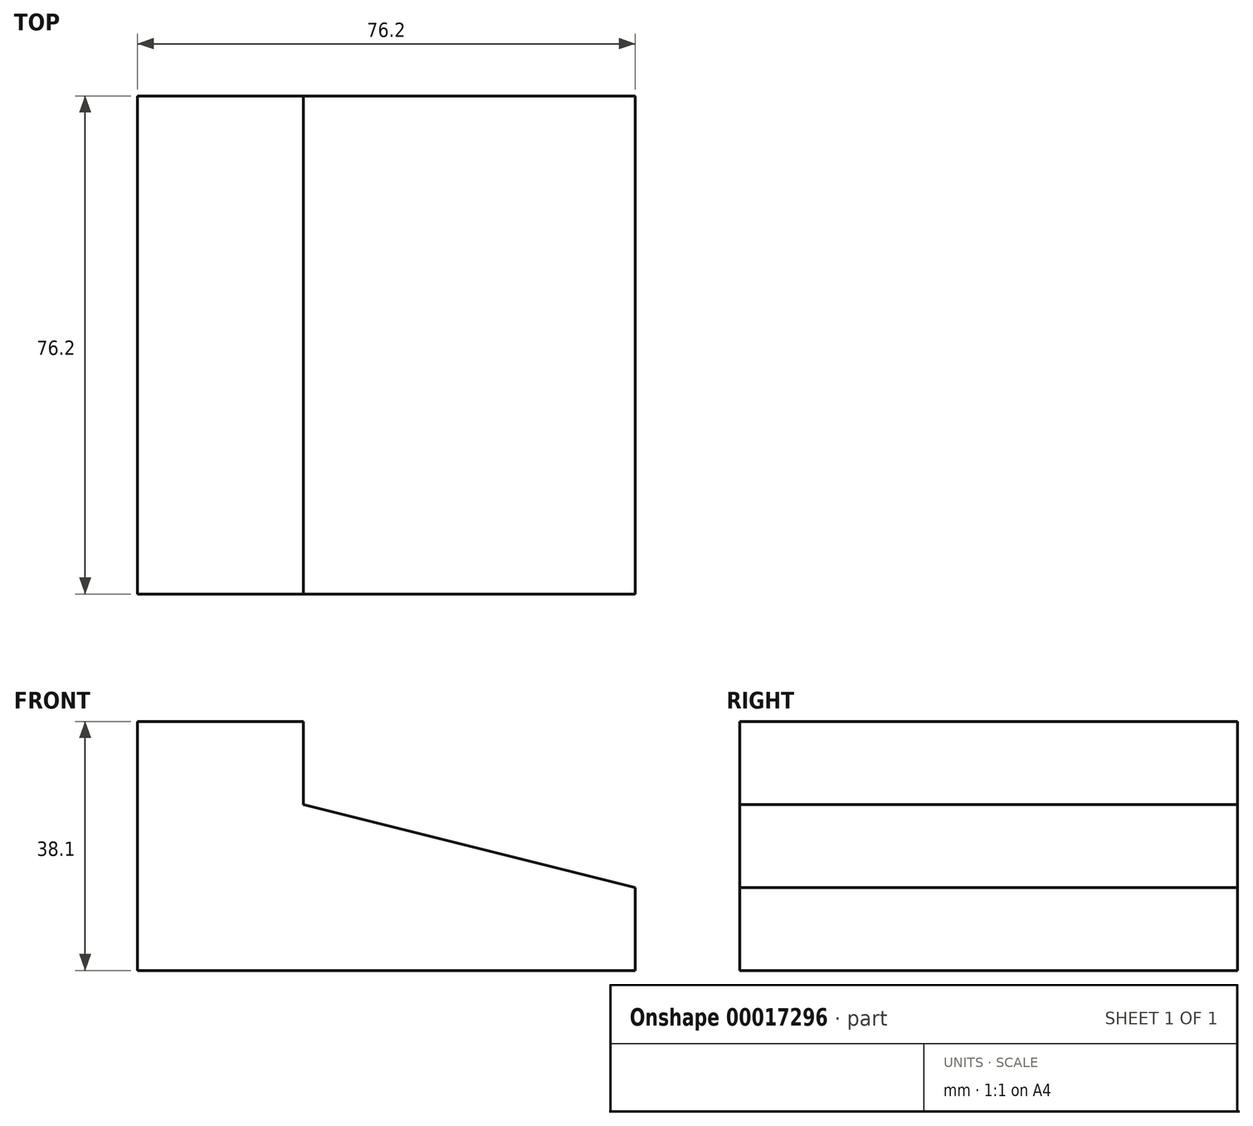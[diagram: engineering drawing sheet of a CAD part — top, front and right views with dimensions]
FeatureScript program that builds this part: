
annotation { "Feature Type Name" : "Feature", "Feature Type Description" : "" }
export const myFeature = defineFeature(function(context is Context, id is Id, definition is map)
    precondition{}
    {
        {
            var Q0;
            Q0=qCreatedBy(makeId("Front.planeOp"),FACE);
            var sketch = newSketch(context, id + "F0", { "sketchPlane" : qUnion([Q0])});
            skLineSegment(sketch, "E0", {"start": v(-49.67, 25.4) * mm, "end": v(-49.67, -12.7) * mm});
            skLineSegment(sketch, "E1", {"start": v(-49.67, 25.4) * mm, "end": v(-24.27, 25.4) * mm});
            skLineSegment(sketch, "E2", {"start": v(-24.27, 25.4) * mm, "end": v(-24.27, 12.7) * mm});
            skLineSegment(sketch, "E3", {"start": v(-49.67, -12.7) * mm, "end": v(26.53, -12.7) * mm});
            skLineSegment(sketch, "E4", {"start": v(26.53, -12.7) * mm, "end": v(26.53, 0) * mm});
            skLineSegment(sketch, "E5", {"start": v(-24.27, 12.7) * mm, "end": v(26.53, 0) * mm});
            skSolve(sketch);
        }
        {
            var Q0;
            Q0=makeQuery(id+"F0.imprint","IMPRINT",FACE,{"disambiguationData":[TD([[makeQuery(id+"F0.imprint","IMPRINT",EDGE,{"derivedFrom":sQuery(id+"F0.wireOp",EDGE,"E0")}),1.0]])]});
            extrude(context, id + "F1", {"entities" : qUnion([Q0]), "depth" : 76.2 * mm});
        }
    });
